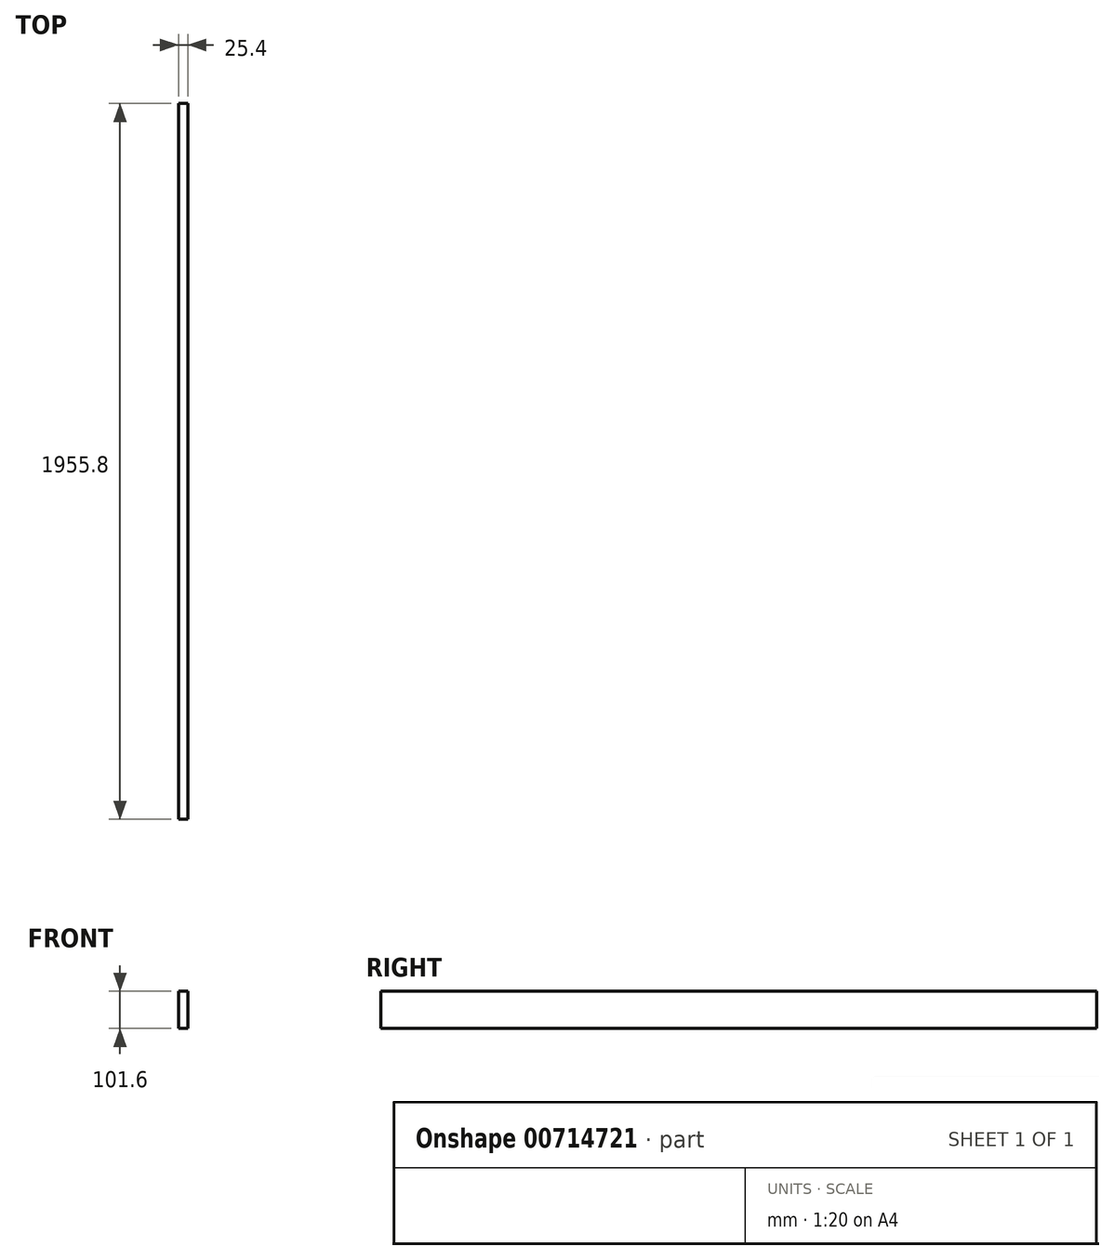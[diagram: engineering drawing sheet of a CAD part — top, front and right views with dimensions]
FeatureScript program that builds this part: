
annotation { "Feature Type Name" : "Feature", "Feature Type Description" : "" }
export const myFeature = defineFeature(function(context is Context, id is Id, definition is map)
    precondition{}
    {
        {
            var Q0;
            Q0=qCreatedBy(makeId("Right.planeOp"),FACE);
            var sketch = newSketch(context, id + "F0", { "sketchPlane" : qUnion([Q0])});
            skLineSegment(sketch, "E0.bottom", {"start": v(1955.8, 101.6) * mm, "end": v(0, 101.6) * mm});
            skLineSegment(sketch, "E0.top", {"start": v(1955.8, 0) * mm, "end": v(0, 0) * mm});
            skLineSegment(sketch, "E0.left", {"start": v(1955.8, 101.6) * mm, "end": v(1955.8, 0) * mm});
            skLineSegment(sketch, "E0.right", {"start": v(0, 101.6) * mm, "end": v(0, 0) * mm});
            skSolve(sketch);
        }
        {
            var Q0;
            Q0=makeQuery(id+"F0.imprint","IMPRINT",FACE,{"disambiguationData":[TD([[makeQuery(id+"F0.imprint","IMPRINT",EDGE,{"derivedFrom":sQuery(id+"F0.wireOp",EDGE,"E0.bottom")}),1.0]])]});
            extrude(context, id + "F1", {"entities" : qUnion([Q0]), "depth" : 25.4 * mm, "offsetDistance" : 25.4 * mm});
        }
    });
